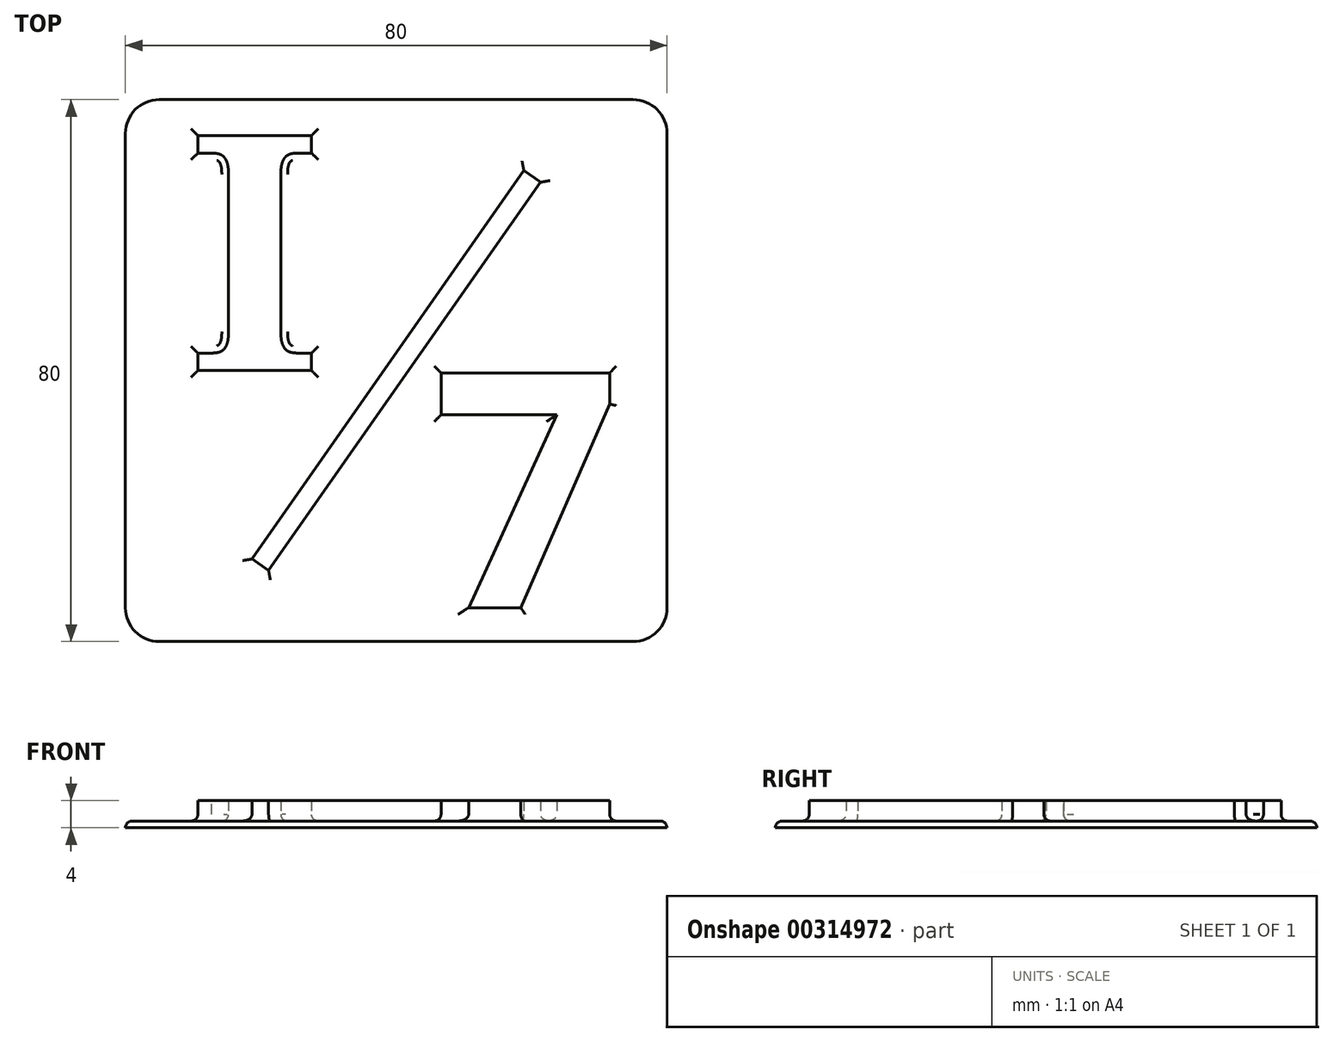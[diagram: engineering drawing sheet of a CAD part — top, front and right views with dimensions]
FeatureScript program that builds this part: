
annotation { "Feature Type Name" : "Feature", "Feature Type Description" : "" }
export const myFeature = defineFeature(function(context is Context, id is Id, definition is map)
    precondition{}
    {
        {
            var Q0;
            Q0=qCreatedBy(makeId("Top.planeOp"),FACE);
            var sketch = newSketch(context, id + "F0", { "sketchPlane" : qUnion([Q0])});
            skLineSegment(sketch, "E0.bottom", {"start": v(35, -40) * mm, "end": v(-35, -40) * mm});
            skLineSegment(sketch, "E0.top", {"start": v(35, 40) * mm, "end": v(-35, 40) * mm});
            skLineSegment(sketch, "E0.left", {"start": v(40, -35) * mm, "end": v(40, 35) * mm});
            skLineSegment(sketch, "E0.right", {"start": v(-40, -35) * mm, "end": v(-40, 35) * mm});
            skPoint(sketch, "E0.middle", {"position": v(0, 0) * mm});
            skPoint(sketch, "E1.visualSharp", {"position": v(-40, 40) * mm});
            skArc(sketch, "E1.filletArc", {"start": v(-35, 40) * mm, "mid": v(-38.54, 38.54) * mm, "end": v(-40, 35) * mm});
            skPoint(sketch, "E2.visualSharp", {"position": v(40, 40) * mm});
            skArc(sketch, "E2.filletArc", {"start": v(40, 35) * mm, "mid": v(38.54, 38.54) * mm, "end": v(35, 40) * mm});
            skPoint(sketch, "E3.visualSharp", {"position": v(40, -40) * mm});
            skArc(sketch, "E3.filletArc", {"start": v(35, -40) * mm, "mid": v(38.54, -38.54) * mm, "end": v(40, -35) * mm});
            skPoint(sketch, "E4.visualSharp", {"position": v(-40, -40) * mm});
            skArc(sketch, "E4.filletArc", {"start": v(-40, -35) * mm, "mid": v(-38.54, -38.54) * mm, "end": v(-35, -40) * mm});
            skLineSegment(sketch, "E5", {"start": v(0, 40) * mm, "end": v(0, -40) * mm, "construction": true});
            skLineSegment(sketch, "E6", {"start": v(40, 0) * mm, "end": v(-40, 0) * mm, "construction": true});
            skText(sketch, "E7", { "text": "I", "fontName": "NotoSerif-Bold.ttf"});
            skLineSegment(sketch, "E8", {"start": v(-20, 40) * mm, "end": v(-20, -40) * mm, "construction": true});
            skText(sketch, "E9", { "text": "7", "fontName": "OpenSans-Bold.ttf"});
            skLineSegment(sketch, "E10", {"start": v(20, 40) * mm, "end": v(20, -40) * mm, "construction": true});
            skLineSegment(sketch, "E11", {"start": v(18.85, 29.53) * mm, "end": v(-21.3, -27.8) * mm});
            skLineSegment(sketch, "E12", {"start": v(-21.3, -27.8) * mm, "end": v(-18.85, -29.53) * mm});
            skLineSegment(sketch, "E13", {"start": v(-18.85, -29.53) * mm, "end": v(21.3, 27.8) * mm});
            skLineSegment(sketch, "E14", {"start": v(18.85, 29.53) * mm, "end": v(21.3, 27.8) * mm});
            const initialGuessF0  = {"E7": [-0.03065, 0, 1, 0, 0.035], "E9": [0.00532, -0.035, 1, 0, 0.035]};
            skSetInitialGuess(sketch, initialGuessF0);
            skSolve(sketch);
        }
        {
            var Q0;
            Q0=makeQuery(id+"F0.imprint","IMPRINT",FACE,{"disambiguationData":[TD([[makeQuery(id+"F0.imprint","IMPRINT",EDGE,{"derivedFrom":sQuery(id+"F0.wireOp",EDGE,"E0.bottom")}),-1.0]])]});
            var Q1;
            Q1=makeQuery(id+"F0.imprint","IMPRINT",FACE,{"disambiguationData":[TD([[makeQuery(id+"F0.imprint","IMPRINT",EDGE,{"derivedFrom":sQuery(id+"F0.wireOp",EDGE,"E7.sketch_text.stroke-0")}),-1.0]])]});
            var Q2;
            Q2=makeQuery(id+"F0.imprint","IMPRINT",FACE,{"disambiguationData":[TD([[makeQuery(id+"F0.imprint","IMPRINT",EDGE,{"derivedFrom":sQuery(id+"F0.wireOp",EDGE,"E11")}),1.0]])]});
            var Q3;
            Q3=makeQuery(id+"F0.imprint","IMPRINT",FACE,{"disambiguationData":[TD([[makeQuery(id+"F0.imprint","IMPRINT",EDGE,{"derivedFrom":sQuery(id+"F0.wireOp",EDGE,"E9.sketch_text.stroke-0")}),-1.0]])]});
            extrude(context, id + "F1", {"entities" : qUnion([Q0, Q1, Q2, Q3]), "oppositeDirection" : true, "depth" : 1 * mm});
        }
        {
            var Q0;
            Q0=makeQuery(id+"F0.imprint","IMPRINT",FACE,{"disambiguationData":[TD([[makeQuery(id+"F0.imprint","IMPRINT",EDGE,{"derivedFrom":sQuery(id+"F0.wireOp",EDGE,"E7.sketch_text.stroke-0")}),-1.0]])]});
            var Q1;
            Q1=makeQuery(id+"F0.imprint","IMPRINT",FACE,{"disambiguationData":[TD([[makeQuery(id+"F0.imprint","IMPRINT",EDGE,{"derivedFrom":sQuery(id+"F0.wireOp",EDGE,"E11")}),1.0]])]});
            var Q2;
            Q2=makeQuery(id+"F0.imprint","IMPRINT",FACE,{"disambiguationData":[TD([[makeQuery(id+"F0.imprint","IMPRINT",EDGE,{"derivedFrom":sQuery(id+"F0.wireOp",EDGE,"E9.sketch_text.stroke-0")}),-1.0]])]});
            extrude(context, id + "F2", {"entities" : qUnion([Q0, Q1, Q2]), "operationType" : NewBodyOperationType.ADD, "depth" : 3 * mm});
        }
        {
            var Q0;
            Q0=makeQuery(id+"F1.opExtrude","CAP_FACE",FACE,{"disambiguationData":[OSD([sQuery(id+"F0.wireOp",EDGE,"E0.bottom"),sQuery(id+"F0.wireOp",EDGE,"E0.top"),sQuery(id+"F0.wireOp",EDGE,"E0.left"),sQuery(id+"F0.wireOp",EDGE,"E0.right"),sQuery(id+"F0.wireOp",EDGE,"E1.filletArc"),sQuery(id+"F0.wireOp",EDGE,"E2.filletArc"),sQuery(id+"F0.wireOp",EDGE,"E3.filletArc"),sQuery(id+"F0.wireOp",EDGE,"E4.filletArc")])],"isStart":true});
            fillet(context, id + "F3", {"entities" : qUnion([Q0]), "radius" : 1 * mm, "tangentPropagation" : true, "allowEdgeOverflow" : false});
        }
    });
